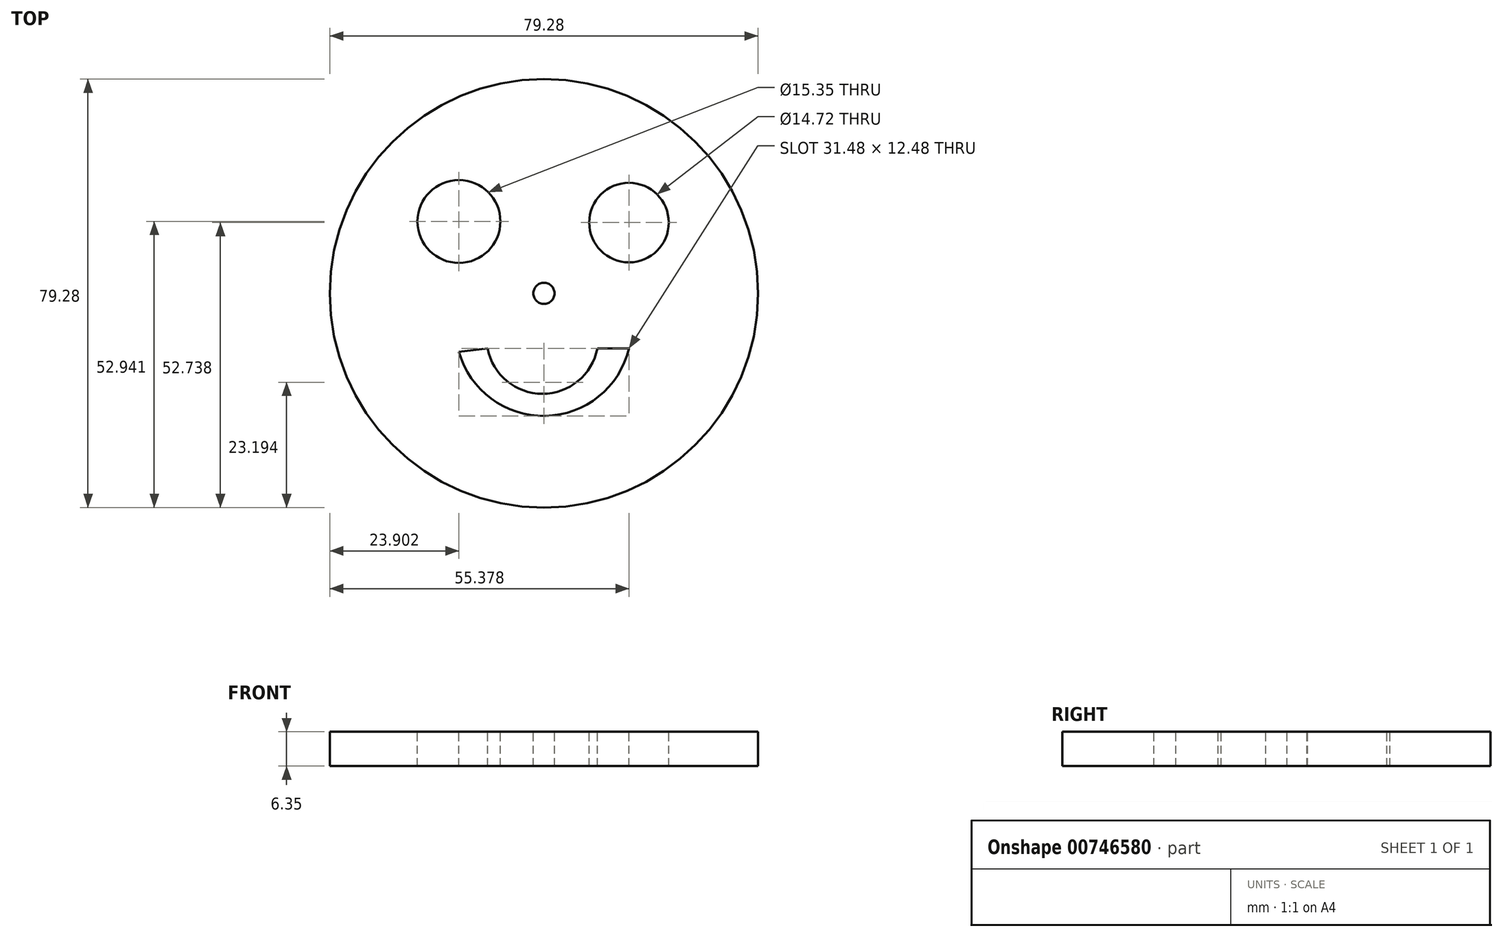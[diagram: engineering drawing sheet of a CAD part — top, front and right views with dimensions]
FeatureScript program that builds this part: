
annotation { "Feature Type Name" : "Feature", "Feature Type Description" : "" }
export const myFeature = defineFeature(function(context is Context, id is Id, definition is map)
    precondition{}
    {
        {
            var Q0;
            Q0=qCreatedBy(makeId("Top.planeOp"),FACE);
            var sketch = newSketch(context, id + "F0", { "sketchPlane" : qUnion([Q0])});
            skCircle(sketch, "E0", {"center": v(0, 0) * mm, "radius": 39.64 * mm});
            skSolve(sketch);
        }
        {
            var Q0;
            Q0 = qSketchRegion(id + "F0", true);
            extrude(context, id + "F1", {"entities" : qUnion([Q0]), "depth" : 6.35 * mm, "offsetDistance" : 25.4 * mm});
        }
        {
            var Q0;
            Q0=makeQuery(id+"F1.opExtrude","CAP_FACE",FACE,{"disambiguationData":[OSD([sQuery(id+"F0.wireOp",EDGE,"E0")])],"isStart":false});
            var sketch = newSketch(context, id + "F2", { "sketchPlane" : qUnion([Q0])});
            skCircle(sketch, "E1", {"center": v(-15.74, 13.3) * mm, "radius": 7.68 * mm});
            skCircle(sketch, "E2", {"center": v(15.74, 13.1) * mm, "radius": 7.36 * mm});
            skCircle(sketch, "E3", {"center": v(0, 0) * mm, "radius": 1.95 * mm});
            skArc(sketch, "E4", {"start": v(-15.74, -10.81) * mm, "mid": v(0.24, -22.69) * mm, "end": v(15.74, -10.2) * mm});
            skArc(sketch, "E5", {"start": v(-10.43, -10.2) * mm, "mid": v(-0.28, -18.6) * mm, "end": v(9.88, -10.2) * mm});
            skLineSegment(sketch, "E6", {"start": v(-15.74, -10.81) * mm, "end": v(-10.43, -10.2) * mm});
            skLineSegment(sketch, "E7", {"start": v(9.88, -10.2) * mm, "end": v(15.74, -10.2) * mm});
            skSolve(sketch);
        }
        {
            var Q0;
            Q0 = qSketchRegion(id + "F2", true);
            extrude(context, id + "F3", {"entities" : qUnion([Q0]), "operationType" : NewBodyOperationType.REMOVE, "endBound" : BoundingType.THROUGH_ALL, "oppositeDirection" : true, "depth" : 25.4 * mm, "offsetDistance" : 25.4 * mm});
        }
    });
